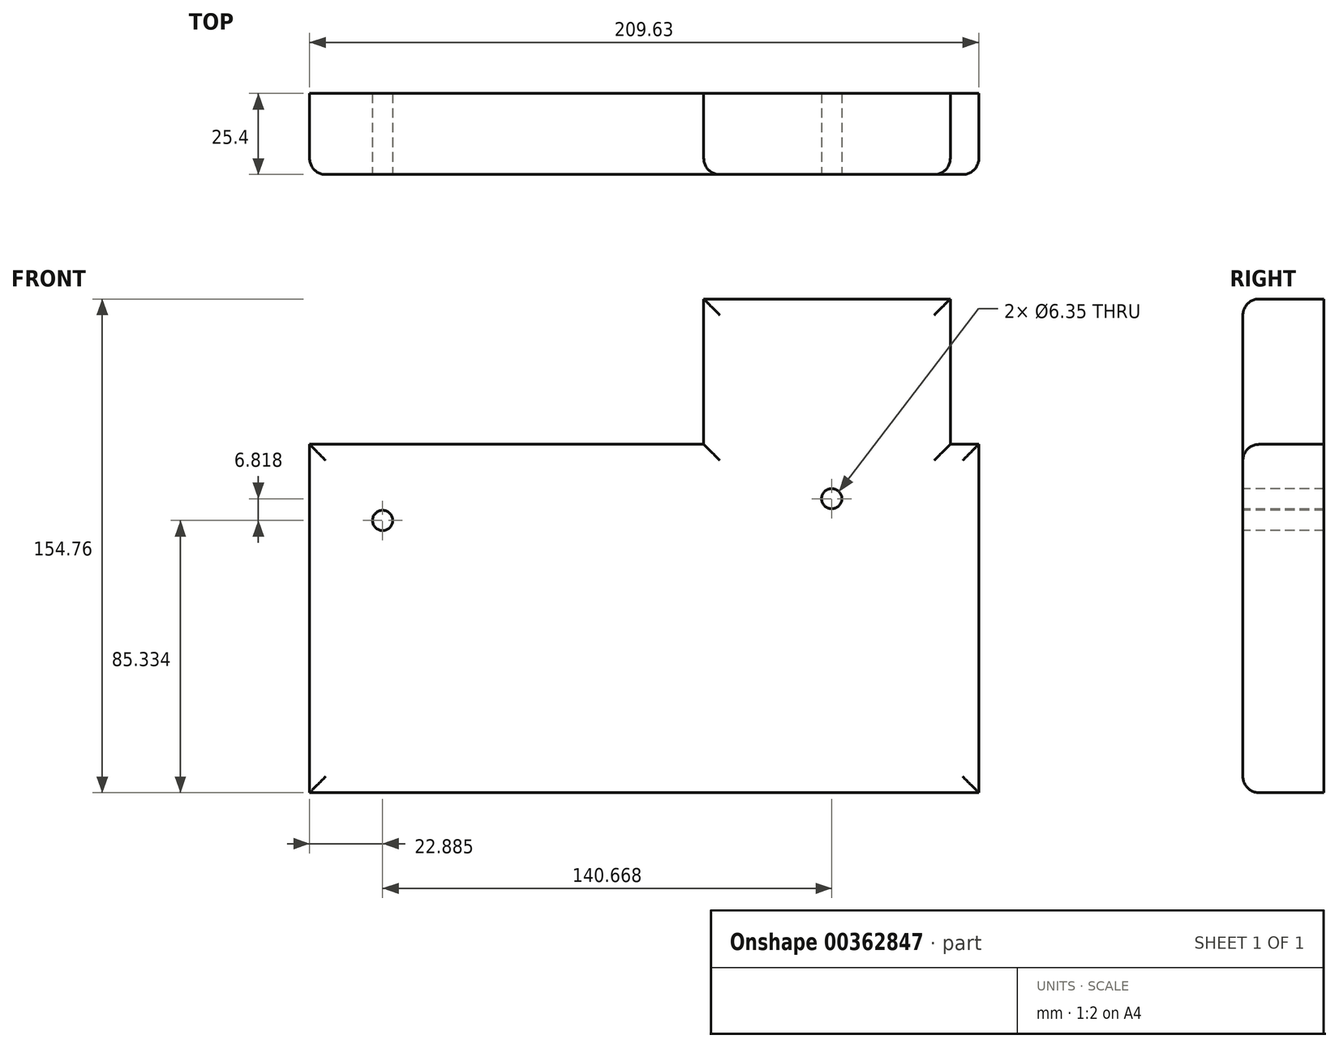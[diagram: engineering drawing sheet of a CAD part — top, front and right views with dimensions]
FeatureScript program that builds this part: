
annotation { "Feature Type Name" : "Feature", "Feature Type Description" : "" }
export const myFeature = defineFeature(function(context is Context, id is Id, definition is map)
    precondition{}
    {
        {
            var Q0;
            Q0=qCreatedBy(makeId("Front.planeOp"),FACE);
            var sketch = newSketch(context, id + "F0", { "sketchPlane" : qUnion([Q0])});
            skLineSegment(sketch, "E0.bottom", {"start": v(-120.2, 45.99) * mm, "end": v(-143.18, 45.99) * mm});
            skLineSegment(sketch, "E0.top", {"start": v(-120.2, 90.7) * mm, "end": v(-143.18, 90.7) * mm});
            skLineSegment(sketch, "E0.left", {"start": v(-120.2, 45.99) * mm, "end": v(-120.2, 90.7) * mm});
            skLineSegment(sketch, "E0.right", {"start": v(-143.18, 45.99) * mm, "end": v(-143.18, 90.7) * mm});
            skPoint(sketch, "E1.oppositeSnap0", {"position": v(-131.69, 90.7) * mm});
            skLineSegment(sketch, "E1.bottom", {"start": v(-120.2, 68.34) * mm, "end": v(-100.4, 68.34) * mm});
            skLineSegment(sketch, "E1.top", {"start": v(-120.2, 90.7) * mm, "end": v(-100.4, 90.7) * mm});
            skLineSegment(sketch, "E1.left", {"start": v(-120.2, 68.34) * mm, "end": v(-120.2, 90.7) * mm});
            skLineSegment(sketch, "E1.right", {"start": v(-100.4, 68.34) * mm, "end": v(-100.4, 90.7) * mm});
            skLineSegment(sketch, "E2.bottom", {"start": v(-100.4, 45.13) * mm, "end": v(109.23, 45.13) * mm});
            skLineSegment(sketch, "E2.top", {"start": v(-100.4, -64.06) * mm, "end": v(109.23, -64.06) * mm});
            skLineSegment(sketch, "E2.left", {"start": v(-100.4, 45.13) * mm, "end": v(-100.4, -64.06) * mm});
            skLineSegment(sketch, "E2.right", {"start": v(109.23, 45.13) * mm, "end": v(109.23, -64.06) * mm});
            skLineSegment(sketch, "E3.bottom", {"start": v(23.07, 7.74) * mm, "end": v(100.3, 7.74) * mm});
            skLineSegment(sketch, "E3.top", {"start": v(23.07, 90.7) * mm, "end": v(100.3, 90.7) * mm});
            skLineSegment(sketch, "E3.left", {"start": v(23.07, 7.74) * mm, "end": v(23.07, 90.7) * mm});
            skLineSegment(sketch, "E3.right", {"start": v(100.3, 7.74) * mm, "end": v(100.3, 90.7) * mm});
            skLineSegment(sketch, "E4.bottom", {"start": v(74.03, 77.62) * mm, "end": v(88.22, 77.62) * mm});
            skLineSegment(sketch, "E4.top", {"start": v(74.03, 90.7) * mm, "end": v(88.22, 90.7) * mm});
            skLineSegment(sketch, "E4.left", {"start": v(74.03, 77.62) * mm, "end": v(74.03, 90.7) * mm});
            skLineSegment(sketch, "E4.right", {"start": v(88.22, 77.62) * mm, "end": v(88.22, 90.7) * mm});
            skSolve(sketch);
        }
        {
            var Q0;
            Q0 = qSketchRegion(id + "F0", true);
            extrude(context, id + "F1", {"entities" : qUnion([Q0]), "depth" : 25.4 * mm});
        }
        {
            var Q0;
            Q0=makeQuery(id+"F1.opExtrude","CAP_FACE",FACE,{"disambiguationData":[OSD([sQuery(id+"F0.wireOp",EDGE,"E2.bottom"),sQuery(id+"F0.wireOp",EDGE,"E2.top"),sQuery(id+"F0.wireOp",EDGE,"E2.left"),sQuery(id+"F0.wireOp",EDGE,"E2.right"),sQuery(id+"F0.wireOp",EDGE,"E3.top"),sQuery(id+"F0.wireOp",EDGE,"E3.left"),sQuery(id+"F0.wireOp",EDGE,"E3.right"),sQuery(id+"F0.wireOp",EDGE,"E4.top")])],"isStart":false});
            fillet(context, id + "F2", {"entities" : qUnion([Q0]), "radius" : 5.08 * mm, "tangentPropagation" : true, "allowEdgeOverflow" : false});
        }
        {
            var Q0;
            Q0=makeQuery(id+"F1.opExtrude","SWEPT_BODY",BODY,{"disambiguationData":[OSD([sQuery(id+"F0.wireOp",EDGE,"E0.bottom"),sQuery(id+"F0.wireOp",EDGE,"E0.top"),sQuery(id+"F0.wireOp",EDGE,"E0.left"),sQuery(id+"F0.wireOp",EDGE,"E0.right"),sQuery(id+"F0.wireOp",EDGE,"E1.bottom"),sQuery(id+"F0.wireOp",EDGE,"E1.top"),sQuery(id+"F0.wireOp",EDGE,"E1.right")])]});
            deleteBodies(context, id + "F3", {"entities" : qUnion([Q0])});
        }
        {
            var Q0;
            Q0=qCreatedBy(makeId("Front.planeOp"),FACE);
            var sketch = newSketch(context, id + "F4", { "sketchPlane" : qUnion([Q0])});
            skCircle(sketch, "E5", {"center": v(-73.59, -5.02) * mm, "radius": 14.51 * mm});
            skSolve(sketch);
        }
        {
            var Q0;
            Q0 = qSketchRegion(id + "F4", true);
            extrude(context, id + "F5", {"entities" : qUnion([Q0]), "operationType" : NewBodyOperationType.ADD, "depth" : 4.06 * mm});
        }
        {
            var Q0;
            Q0=makeQuery(id+"F1.opExtrude","CAP_FACE",FACE,{"disambiguationData":[OSD([sQuery(id+"F0.wireOp",EDGE,"E2.bottom"),sQuery(id+"F0.wireOp",EDGE,"E2.top"),sQuery(id+"F0.wireOp",EDGE,"E2.left"),sQuery(id+"F0.wireOp",EDGE,"E2.right"),sQuery(id+"F0.wireOp",EDGE,"E3.top"),sQuery(id+"F0.wireOp",EDGE,"E3.left"),sQuery(id+"F0.wireOp",EDGE,"E3.right"),sQuery(id+"F0.wireOp",EDGE,"E4.top")])],"isStart":false});
            var sketch = newSketch(context, id + "F6", { "sketchPlane" : qUnion([Q0])});
            skPoint(sketch, "E6", {"position": v(-77.52, 21.27) * mm});
            skPoint(sketch, "E7", {"position": v(63.15, 28.1) * mm});
            skSolve(sketch);
        }
        {
            var Q0;
            Q0=sQuery(id+"F6.wireOp",VERTEX,"E6");
            var Q1;
            Q1=sQuery(id+"F6.wireOp",VERTEX,"E7");
            var Q2;
            Q2=makeQuery(id+"F1.opExtrude","SWEPT_BODY",BODY,{"disambiguationData":[OSD([sQuery(id+"F0.wireOp",EDGE,"E2.bottom"),sQuery(id+"F0.wireOp",EDGE,"E2.top"),sQuery(id+"F0.wireOp",EDGE,"E2.left"),sQuery(id+"F0.wireOp",EDGE,"E2.right"),sQuery(id+"F0.wireOp",EDGE,"E3.top"),sQuery(id+"F0.wireOp",EDGE,"E3.left"),sQuery(id+"F0.wireOp",EDGE,"E3.right"),sQuery(id+"F0.wireOp",EDGE,"E4.top")])]});
            hole(context, id + "F7", {"style" : HoleStyle.SIMPLE, "endStyle" : HoleEndStyle.THROUGH, "holeDiameter" : 6.35 * mm, "isTappedThrough" : true, "tappedDepth" : 12.7 * mm, "tapClearance" : 3, "locations" : qUnion([Q0, Q1]), "scope" : qUnion([Q2])});
        }
    });
